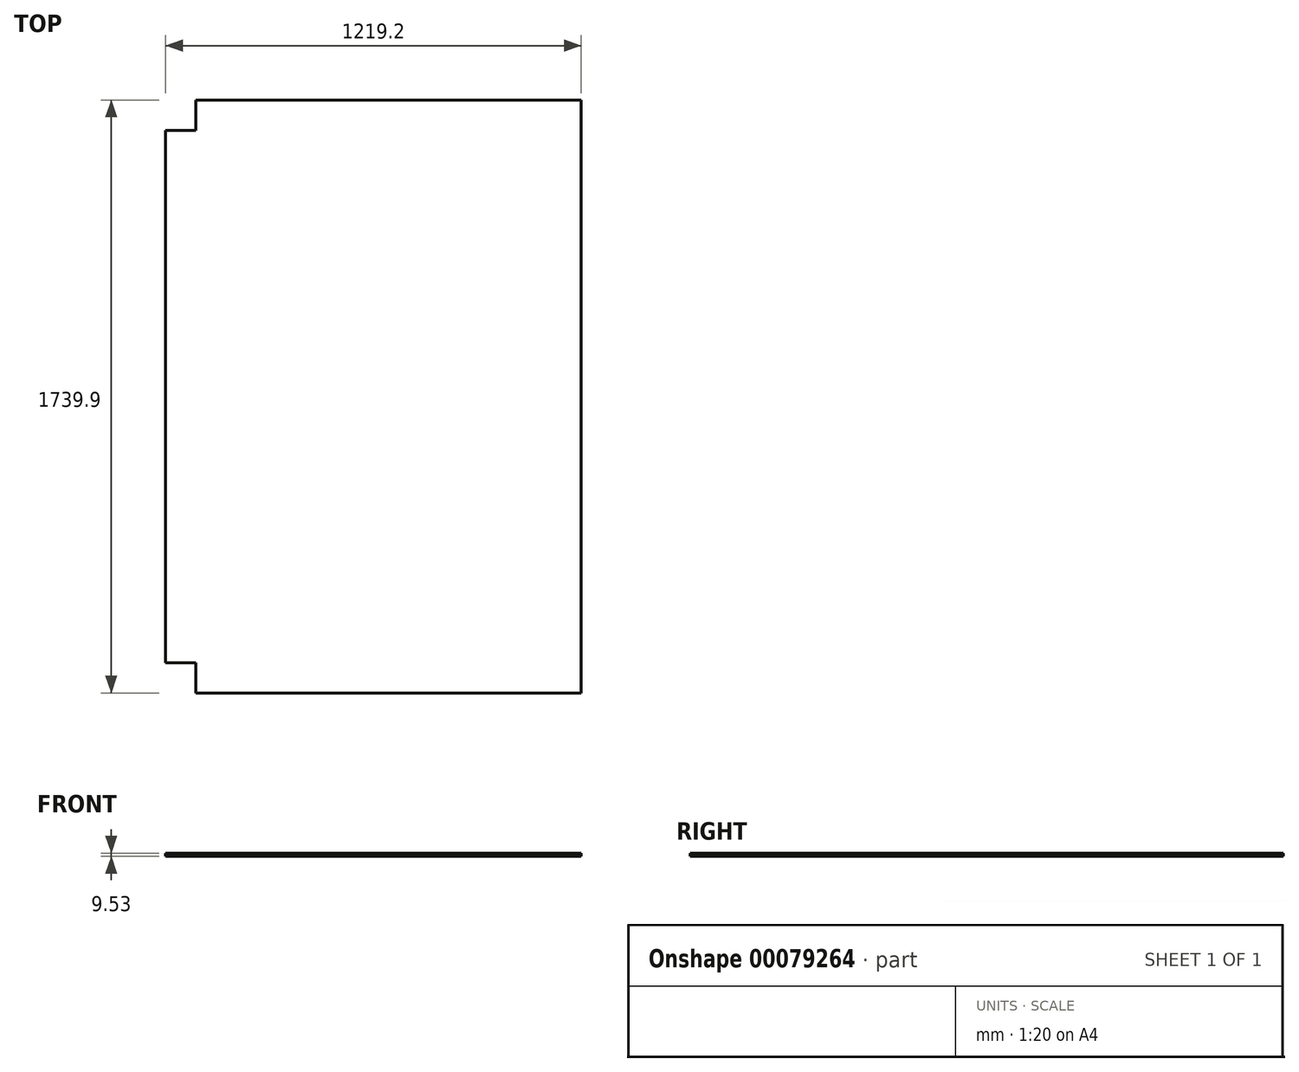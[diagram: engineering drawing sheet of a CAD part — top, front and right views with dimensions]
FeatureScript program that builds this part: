
annotation { "Feature Type Name" : "Feature", "Feature Type Description" : "" }
export const myFeature = defineFeature(function(context is Context, id is Id, definition is map)
    precondition{}
    {
        {
            var Q0;
            Q0=qCreatedBy(makeId("Top.planeOp"),FACE);
            var sketch = newSketch(context, id + "F0", { "sketchPlane" : qUnion([Q0])});
            skLineSegment(sketch, "E0", {"start": v(0, 0) * mm, "end": v(0, 1739.9) * mm});
            skLineSegment(sketch, "E1", {"start": v(0, 1739.9) * mm, "end": v(-1130.3, 1739.9) * mm});
            skLineSegment(sketch, "E2", {"start": v(-1130.3, 1739.9) * mm, "end": v(-1130.3, 1651) * mm});
            skLineSegment(sketch, "E3", {"start": v(-1130.3, 1651) * mm, "end": v(-1219.2, 1651) * mm});
            skLineSegment(sketch, "E4", {"start": v(-1219.2, 1651) * mm, "end": v(-1219.2, 88.9) * mm});
            skLineSegment(sketch, "E5", {"start": v(-1219.2, 88.9) * mm, "end": v(-1130.3, 88.9) * mm});
            skLineSegment(sketch, "E6", {"start": v(-1130.3, 88.9) * mm, "end": v(-1130.3, 0) * mm});
            skLineSegment(sketch, "E7", {"start": v(-1130.3, 0) * mm, "end": v(0, 0) * mm});
            skSolve(sketch);
        }
        {
            var Q0;
            Q0=makeQuery(id+"F0.imprint","IMPRINT",FACE,{"disambiguationData":[TD([[makeQuery(id+"F0.imprint","IMPRINT",EDGE,{"derivedFrom":sQuery(id+"F0.wireOp",EDGE,"E0")}),1.0]])]});
            extrude(context, id + "F1", {"entities" : qUnion([Q0]), "depth" : 9.52 * mm});
        }
    });
